# Revit family: xxxDrinking_Fountain-Wall_Mounted-Murdock_Mfg-A171-UG-VR_Series
name_source: partatom
category: Plumbing Fixtures
units: mm (PartAtom-declared; Revit-internal decimal feet)

## family parameters
Cut with Voids When Loaded = Yes
Host = Face
OmniClass Number = 23.65.70.14.11
OmniClass Title = Drinking Fountains/Coolers
Part Type = Normal
Room Calculation Point = No
Round Connector Dimension = Use Diameter
Shared = Yes

## types (4) — shared parameters
-BP8 Back Panel, Stainless Steel = No
-CSC5 Concealed Support Carrier = No
-DD Drop Down Door = No
-LOGO Customer Specified Logo / Graphics = No
-WF1 = No
-WF3 = No
ADA Compliant = Yes
Activation = Push Button
Assembly Code = A171100F-UG-VR
CW Connection = Yes
CWFU = 1
Cold Water Connection Diameter = 3/8"
Cold Water Connection Height = 19 3/8"
Cold Water Connection Width = 2"
Default Elevation = 0"
Description = Barrier-Free, Vandal Resistant Button, Wall Mounted- No Refrigeration Drinking Fountain
Finish = Stainless Steel-Murdock-Type 304-Satin
Finish- Push Button = Brass-Murdock-Chrome Plated
HW Connection = No
Height From Floor Level = 33"
IAPMO Compliance = NSF/ANSI 61 & Federal Public Law 111-380 (No lead)
Installation Instruction Link = https://www.murdockmfg.com
Installation Type = Wall Mounted
Length = 18 1/2"
Manufacturer = Murdock Manufacturing
Material = Stainless Steel-Murdock-Type 304-Satin
Price = Prices may vary. Please consult Manufacturer Representative for most up-to-date price list.
Product Documentation Link = https://www.murdockmfg.com
Product Page URL = https://www.murdockmfg.com
Revised Date = 02/15/2022
URL = https://www.murdockmfg.com
Vent Connection = No
WFU = 1.5
Waste Connection = Yes
Waste Connection Diameter = 1 1/4"
Waste Connection Height = 22 1/4"
Water Pressure = 20-105 psig
Width = 18 1/2"
cUPC Compliant = Yes
zero-valued in all types: HWFU

## per-type parameters (varying)
| type | Finish- Cabinet | Finish-Bubbler |
| A171100F-UG-VR | Galvanized Steel-Murdock-Powder Coat-Grey | Silicone-Murdock-Grey |
| A171400F-UG-VR | Stainless Steel-Murdock-Type 304-Satin | Silicone-Murdock-Grey |
| A171400S-UG-VR | Stainless Steel-Murdock-Type 304-Satin | Stainless Steel-Murdock-Polished |
| A171100S-UG-VR | Galvanized Steel-Murdock-Powder Coat-Grey | Stainless Steel-Murdock-Polished |

note: column(s) folded — value = type name in every type: Model

## geometry (parser evidence)
native form markers: Sweep x3
no freeform markers — native parametric forms only
